# Revit family: Sirius_FS_400kW_LOD-3
name_source: partatom
category: Mechanical Equipment
revit_build: Autodesk Revit 2014 (Build: 20140709_2115(x64)
units: mm (PartAtom-declared; Revit-internal decimal feet)

## types (1)
- 400kW
    6 Monthly = 0
    Access Clearance Bottom = 250 mm
    Access Clearance Front = 500 mm
    Access Clearance Left = 0 mm  [stored 0 ft]
    Access Clearance Rear = 1000 mm
    Access Clearance Right = 500 mm
    Access Clearance Top = 73 mm
    Additional Technical Details = ww.pottertoncommercial.co.uk/products/stainless-steel/sirius-two-fs-50-110kW.htm
    Air Inlet Connection Size = 80 mm  [stored 0.262467 ft]
    Annually = 0
    BMS Links = Yes
    Bespoke Timeframe = Annual service according to manufacturers guidance.
    Building Regulations Seasonal Efficiency = 93 %
    Burner Control Type = Floor Standing
    CE Mark = 5142180
    Colour = Steel
    Condensate Drain Size = 13 mm
    Condensate Drain Type = Threaded
    Configuration = Space heating
    Control Type = 24
    Daily = http://www.pottertoncommercial.co.uk
    Drain Connection Size = 645 mm
    Drain Connection Type = Threaded
    Embodied Carbon = Y
    Energy Technology List = 0
    Environmental Product Declaration = 0
    ErP Energy Label = 0
    ErP Rated Efficiency at Full Load = 80/60
    ErP Rated Efficiency at Part Load = 87.7 %
    ErP Seasonal Efficiency = 97.7 %
    Expected Life = 0
    External Material = Rectangular (Vertical)
    Features = Cascade kits available for up to 6 boilers
    Finish = White
    Flow and Return Connection Size = 484 mm
    Flow and Return Connection Type = Threaded
    Flue Connection size = 22 mm
    Flue or Air Intake Classification = Plain
    Frequency = 1 Hz
    Fuel Connection Size = 320 mm
    Fuel Connection Type = Stainless Steel
    Full Load Current = 0 A
    Fuse Rating = 0 A
    Gas Consumption rate = Gas - LPG
    Green Guide for Specification = 0
    Gross Weight = 848.00 kg
    Heat Exchanger Material = Condensing
    Heater Operation = Modulating
    Hydraulic Resistance at 11C temperature differential = 0.0
    Hydraulic Resistance at 20C temperature differential = 0.1
    IK Rating = IP21
    IP Rating = 50
    IfcExportAs = IfcBoilerType
    IfcExportType = NOTDEFINED
    Interlocks = Yes
    Life Cycle Analysis = 0
    Location of Manufacturer = 0
    Maintenance Required 0 to 300hrs = 0
    Maintenance Required 1001 to 2000hrs = 0
    Maintenance Required 2001 to 4000hrs = 0
    Maintenance Required 301 to 600hrs = 0
    Maintenance Required 4001 to 8000hrs = 0
    Maintenance Required 601 to 1000hrs = 0
    Maintenance Required 8001 to 12000hrs = 0
    Manufacturer = Potterton Commercial
    Manufacturer Website = Potterton Commercial
    Material Ingredient Reporting = 0
    Maximum Gas Inlet Pressure = 0.0 bar
    Maximum Oil Inlet Pressure = 0.0 bar
    Maximum Operating Pressure = 0.5 bar
    Maximum Power Consumption = 0 W
    Minimum Flow Rate at 11C temperature differential = 0.054 L/s
    Minimum Flow Rate at 20C temperature differential = 0.720 L/s
    Minimum Gas Inlet Pressure = 0.0 bar
    Minimum Oil Inlet Pressure = 0.0 bar
    Minimum Operating Pressure = 4.0 bar
    Minimum Power Consumption = 100 W
    Model = SIRIUS FS400
    Monthly = 0
    Mounting = Powder coated
    NOx Emissions = 9:1
    Nominal Gas Inlet Pressure = 1.0 bar
    Nominal Oil Inlet Pressure = 0.0 bar
    Oil Consumption rate = 0
    Operation and Maintenance Manual = A
    Optional Fuel = Gas - NG
    Overall Height = 600 mm
    Overall Length = 0 mm  [stored 0 ft]
    Overall Width = 681 mm
    Primary Fuel = 61 dBA
    Product Literature = CE-0085CP0089
    Product Model Number = Sirius two FS (50kW)
    Product Range = http://www.pottertoncommercial.co.uk
    Quarterly = 0
    Rated Criteria = 45000
    Rated Output = 0 W
    Reference Standard = C13; C33; B23; B23p; C43; C53; C63; C83
    Responsible Extraction of Materials = https://etl.decc.gov.uk
    Responsible Sourcing of Materials = 0
    Safety Valve Connection Size = 0 mm  [stored 0 ft]
    Safety Valve Connection Type = Plain
    ScheduleType |RF| = Boiler
    Shape = Single boiler
    Shipping Weight = 2.81 kg
    Sound Pressure Level = 125
    Starting Current = 0 A
    Supply Phase = 230
    Turndown Ratio = 96.6 %
    Uniclass2015 = NOTDEFINED
    Voltage = 0 V
    Warranty ID = >10 years
    Water Content = 60.0 L
    Water Treatment Required = No
    Weekly = 0

note: source unit labels omitted for Hydraulic Resistance at 11C temperature differential, Hydraulic Resistance at 20C temperature differential — the stored unit's dimension contradicts the parameter name (converter mislabeling)

note: [stored X ft] marks values corroborated as IEEE doubles in the binary element streams (Revit-internal decimal feet)

## geometry (parser evidence)
native form markers: Blend x2, Sweep x2
no freeform markers — native parametric forms only
